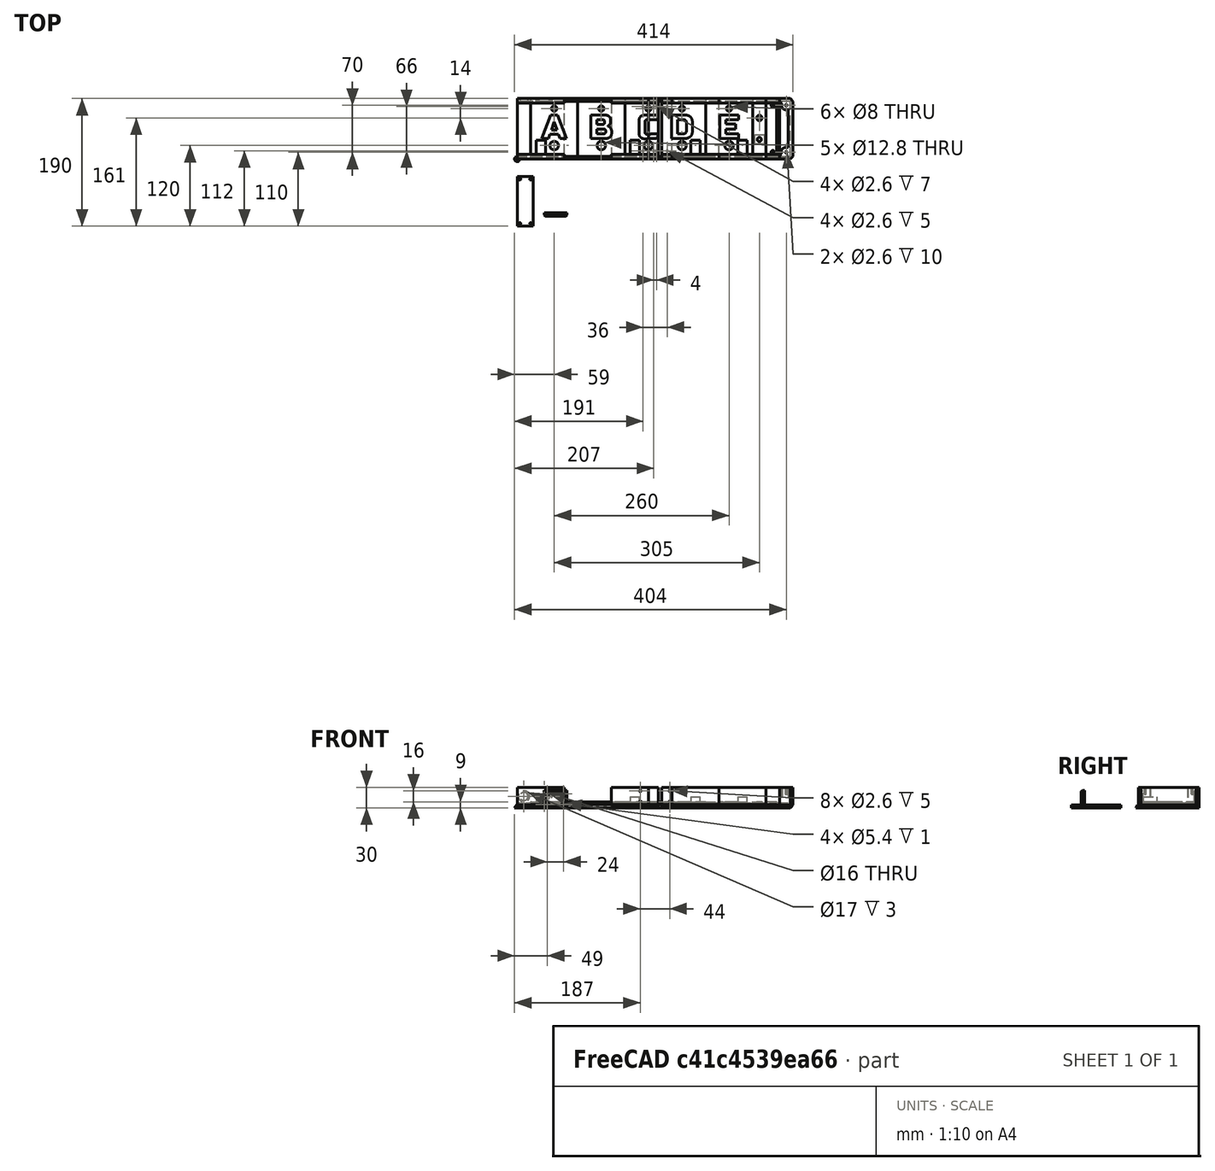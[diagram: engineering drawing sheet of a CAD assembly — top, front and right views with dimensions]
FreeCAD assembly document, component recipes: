
FREECAD ASSEMBLY — COMPONENT RECIPES ("controller")

This assembly document has 4 components, labeled P0..P3 below (a component is one placed body or linked part). 4 of them carry a construction recipe — the FreeCAD feature program that regenerates the part from scratch, quoted from this document or its linked companion documents; the rest are supplied as boundary geometry only. No exploded tour is included for this assembly.
COMPONENT P0 — recipe-attached ("standoff005", modeled in this document).
Construction recipe (the document's own serialized feature program — sketch geometry with constraints, then the solid features built on it; lengths are millimeters unless a unit is written):

FEATURE [Sketcher::SketchObject] Sketch037
  ArcFitTolerance = 1e-06
  AttachmentSupport = -> [XY_Plane030]
  FullyConstrained = true
  MakeInternals = false
  MapMode = 5
  sketch-geometry (1):
    g0: Circle CenterX=0 CenterY=0 CenterZ=0 NormalX=0 NormalY=0 NormalZ=1 AngleXU=0 Radius=4
  constraints (2):
    c: Diameter(g0) = 8
    c: Coincident(g0,g-1)
FEATURE [PartDesign::Plane] DatumPlane
  AttachmentOffset = pos=(0,0,4) rot=(0,0,1;0rad)
  AttachmentSupport = -> [Sketch037]
  Length = 60
  MapMode = 2
  Placement = pos=(0,0,4) rot=(0,0,1;0rad)
  ResizeMode = 0
  Width = 60
FEATURE [Sketcher::SketchObject] Sketch038
  ArcFitTolerance = 1e-06
  AttachmentSupport = -> [DatumPlane]
  FullyConstrained = true
  MakeInternals = false
  MapMode = 5
  Placement = pos=(0,0,4) rot=(0,0,1;0rad)
  sketch-geometry (1):
    g0: Circle CenterX=0 CenterY=0 CenterZ=0 NormalX=0 NormalY=0 NormalZ=1 AngleXU=0 Radius=1.25
  constraints (2):
    c: Diameter(g0) = 2.5
    c: Coincident(g0,g-1)
FEATURE [PartDesign::AdditiveLoft] AdditiveLoft
  Closed = false
  Placement = pos=(0,0,4) rot=(0,0,1;0rad)
  Profile = -> Sketch038
  Refine = true
  Ruled = false
  Sections = -> [Sketch037]
  Suppressed = false
FEATURE [Sketcher::SketchObject] Sketch039
  ArcFitTolerance = 1e-06
  AttachmentSupport = -> [AdditiveLoft]
  FullyConstrained = true
  MakeInternals = false
  MapMode = 5
  Placement = pos=(0,0,4) rot=(0,0,1;0rad)
  sketch-geometry (1):
    g0: Circle CenterX=0 CenterY=0 CenterZ=0 NormalX=0 NormalY=0 NormalZ=1 AngleXU=0 Radius=0.85
  constraints (2):
    c: Diameter(g0) = 1.7
    c: Coincident(g0,g-1)
FEATURE [PartDesign::Pocket] Pocket016
  BaseFeature = -> AdditiveLoft
  Direction = (0,0,-1)
  Length = 5
  Length2 = 5
  Placement = pos=(0,0,4) rot=(0,0,1;0rad)
  Profile = -> Sketch039
  ReferenceAxis = -> Sketch039 [N_Axis]
  Refine = true
  Suppressed = false
  Type = 0
FEATURE [PartDesign::Body] Body023  label="standoff"
  AllowCompound = false
  Group = -> [Sketch037,DatumPlane,Sketch038,AdditiveLoft,Sketch039,Pocket016]
  Origin = -> Origin030
  Tip = -> Pocket016
COMPONENT P1 — same part as P0; its construction recipe is shown at P0.
COMPONENT P2 — same part as P0; its construction recipe is shown at P0.
COMPONENT P3 — same part as P0; its construction recipe is shown at P0.
PROVENANCE & LICENSES
A FreeCAD (.FCStd) document from a public repository crawl; recipes are the document's own serialized feature recipes (and, for linked parts, companion documents' recipes).
License: as declared in the source repository (recorded in the dataset sidecar).
